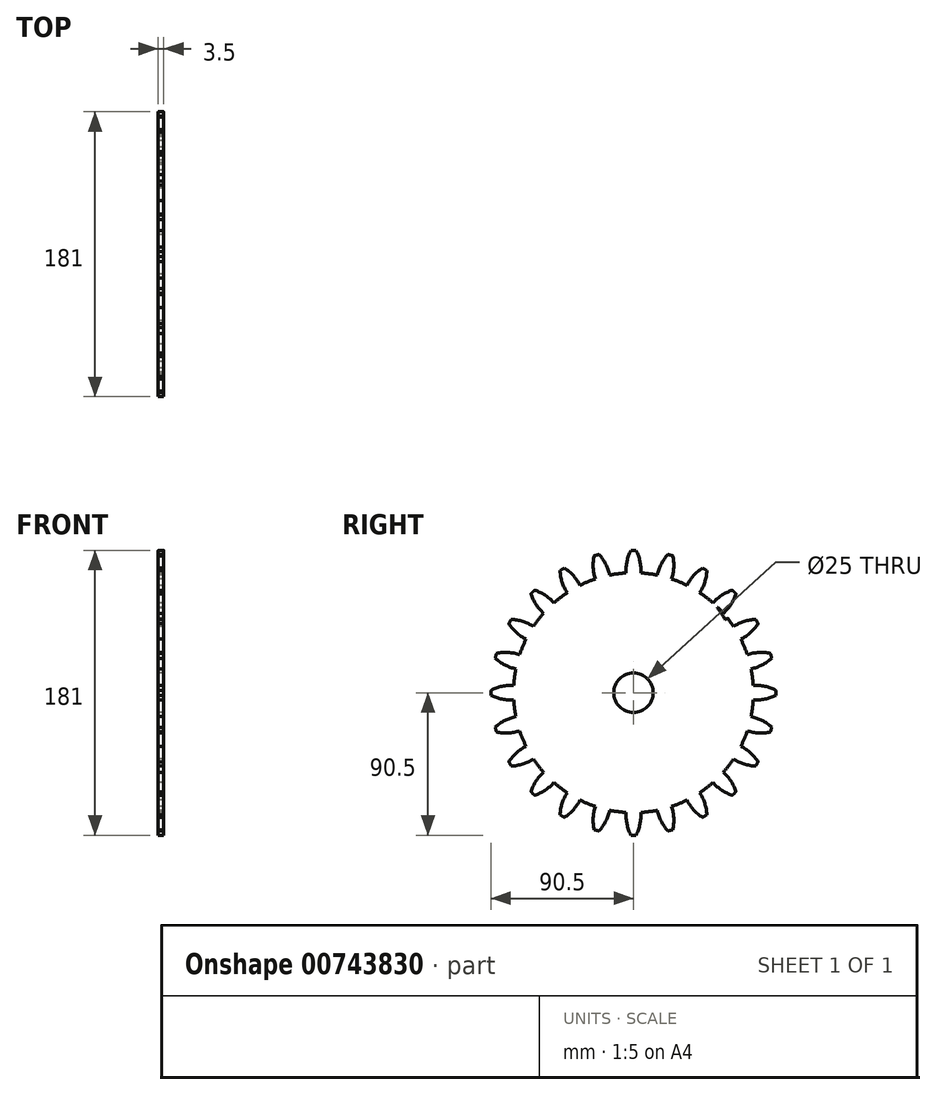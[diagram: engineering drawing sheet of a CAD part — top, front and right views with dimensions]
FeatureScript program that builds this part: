
annotation { "Feature Type Name" : "Feature", "Feature Type Description" : "" }
export const myFeature = defineFeature(function(context is Context, id is Id, definition is map)
    precondition{}
    {
        {
            assignVariable(context, id + "F0", {"name" : "FaceWidth", "anyValue" : 3.5});
        }
        {
            assignVariable(context, id + "F1", {"name" : "NumberTeeth", "anyValue" : 24});
        }
        {
            var Q0;
            Q0=qCreatedBy(makeId("Right.planeOp"),FACE);
            var sketch = newSketch(context, id + "F2", { "sketchPlane" : qUnion([Q0])});
            skCircle(sketch, "E0", {"center": v(0, 0) * mm, "radius": 76.2 * mm});
            skCircle(sketch, "E1", {"center": v(0, 0) * mm, "radius": 12.5 * mm});
            skCircle(sketch, "E2", {"center": v(0, 0) * mm, "radius": 90.5 * mm});
            skPoint(sketch, "E3", {"position": v(0, 76.2) * mm});
            skPoint(sketch, "E4", {"position": v(0, 84.15) * mm});
            skPoint(sketch, "E5", {"position": v(0, 90.5) * mm});
            skLineSegment(sketch, "E6", {"start": v(0, 76.2) * mm, "end": v(0, 84.15) * mm});
            skLineSegment(sketch, "E7", {"start": v(0, 90.5) * mm, "end": v(0, 84.15) * mm});
            skPoint(sketch, "E8", {"position": v(-5.53, 90.33) * mm});
            skLineSegment(sketch, "E9", {"start": v(-5.53, 90.33) * mm, "end": v(0, 0) * mm});
            skArc(sketch, "E10", {"start": v(-1.59, 90.49) * mm, "mid": v(-4.1, 83.48) * mm, "end": v(-4.65, 76.06) * mm});
            skArc(sketch, "E11.MirrorCS", {"start": v(1.59, 90.49) * mm, "mid": v(4.1, 83.48) * mm, "end": v(4.65, 76.06) * mm});
            skLineSegment(sketch, "E12.MirrorCS", {"start": v(5.53, 90.33) * mm, "end": v(0, 0) * mm});
            skPoint(sketch, "E13", {"position": v(-3.88, 84.43) * mm});
            skPoint(sketch, "E14", {"position": v(4.07, 83.64) * mm});
            skArc(sketch, "E15.1.0", {"start": v(-22.57, 89.12) * mm, "mid": v(-23.46, 81.73) * mm, "end": v(-22.35, 74.37) * mm});
            skArc(sketch, "E15.1.1", {"start": v(-19.48, 89.82) * mm, "mid": v(-15.47, 83.55) * mm, "end": v(-13.28, 76.44) * mm});
            skArc(sketch, "E15.2.0", {"start": v(-42.72, 83.1) * mm, "mid": v(-41.95, 75.7) * mm, "end": v(-39.22, 68.78) * mm});
            skArc(sketch, "E15.2.1", {"start": v(-39.86, 84.49) * mm, "mid": v(-34.56, 79.27) * mm, "end": v(-30.84, 72.82) * mm});
            skPoint(sketch, "E15.center", {"position": v(-6, -3.31) * mm});
            skArc(sketch, "E16.3.3.0", {"start": v(-61.03, 72.77) * mm, "mid": v(-58.63, 65.73) * mm, "end": v(-54.43, 59.58) * mm});
            skArc(sketch, "E16.4.3.0", {"start": v(-58.55, 74.75) * mm, "mid": v(-52.22, 70.84) * mm, "end": v(-47.16, 65.38) * mm});
            skArc(sketch, "E16.3.4.0", {"start": v(-76.58, 58.62) * mm, "mid": v(-72.67, 52.28) * mm, "end": v(-67.21, 47.22) * mm});
            skArc(sketch, "E16.4.4.0", {"start": v(-74.6, 61.1) * mm, "mid": v(-67.56, 58.7) * mm, "end": v(-61.41, 54.5) * mm});
            skArc(sketch, "E16.3.5.0", {"start": v(-88.6, 41.36) * mm, "mid": v(-83.37, 36.05) * mm, "end": v(-76.93, 32.33) * mm});
            skArc(sketch, "E16.4.5.0", {"start": v(-87.22, 44.22) * mm, "mid": v(-79.81, 43.44) * mm, "end": v(-72.89, 40.72) * mm});
            skArc(sketch, "E16.3.6.0", {"start": v(-96.46, 21.86) * mm, "mid": v(-90.2, 17.85) * mm, "end": v(-83.08, 15.66) * mm});
            skArc(sketch, "E16.4.6.0", {"start": v(-95.76, 24.95) * mm, "mid": v(-88.37, 25.84) * mm, "end": v(-81, 24.73) * mm});
            skArc(sketch, "E16.3.7.0", {"start": v(-99.8, 1.1) * mm, "mid": v(-92.8, -1.42) * mm, "end": v(-85.37, -1.97) * mm});
            skArc(sketch, "E16.4.7.0", {"start": v(-99.8, 4.27) * mm, "mid": v(-92.8, 6.78) * mm, "end": v(-85.37, 7.33) * mm});
            skArc(sketch, "E16.3.8.0", {"start": v(-98.43, -19.9) * mm, "mid": v(-91.04, -20.78) * mm, "end": v(-83.68, -19.67) * mm});
            skArc(sketch, "E16.4.8.0", {"start": v(-99.13, -16.8) * mm, "mid": v(-92.86, -12.78) * mm, "end": v(-85.75, -10.6) * mm});
            skArc(sketch, "E16.3.9.0", {"start": v(-92.42, -40.04) * mm, "mid": v(-85.02, -39.27) * mm, "end": v(-78.1, -36.54) * mm});
            skArc(sketch, "E16.4.9.0", {"start": v(-93.8, -37.18) * mm, "mid": v(-88.58, -31.88) * mm, "end": v(-82.13, -28.16) * mm});
            skArc(sketch, "E16.3.10.0", {"start": v(-82.08, -58.35) * mm, "mid": v(-75.04, -55.95) * mm, "end": v(-68.89, -51.75) * mm});
            skArc(sketch, "E16.4.10.0", {"start": v(-84.06, -55.87) * mm, "mid": v(-80.15, -49.54) * mm, "end": v(-74.7, -44.48) * mm});
            skArc(sketch, "E16.3.11.0", {"start": v(-67.93, -73.9) * mm, "mid": v(-61.6, -70) * mm, "end": v(-56.53, -64.53) * mm});
            skArc(sketch, "E16.4.11.0", {"start": v(-70.4, -71.92) * mm, "mid": v(-68, -64.88) * mm, "end": v(-63.8, -58.73) * mm});
            skArc(sketch, "E16.3.12.0", {"start": v(-50.67, -85.91) * mm, "mid": v(-45.36, -80.7) * mm, "end": v(-41.64, -74.24) * mm});
            skArc(sketch, "E16.4.12.0", {"start": v(-53.53, -84.54) * mm, "mid": v(-52.75, -77.13) * mm, "end": v(-50.03, -70.2) * mm});
            skArc(sketch, "E16.3.13.0", {"start": v(-31.17, -93.78) * mm, "mid": v(-27.16, -87.51) * mm, "end": v(-24.97, -80.4) * mm});
            skArc(sketch, "E16.4.13.0", {"start": v(-34.26, -93.08) * mm, "mid": v(-35.15, -85.69) * mm, "end": v(-34.04, -78.33) * mm});
            skArc(sketch, "E16.3.14.0", {"start": v(-10.4, -97.12) * mm, "mid": v(-7.89, -90.11) * mm, "end": v(-7.34, -82.69) * mm});
            skArc(sketch, "E16.4.14.0", {"start": v(-13.58, -97.12) * mm, "mid": v(-16.1, -90.11) * mm, "end": v(-16.64, -82.69) * mm});
            skArc(sketch, "E16.3.15.0", {"start": v(10.58, -95.75) * mm, "mid": v(11.47, -88.36) * mm, "end": v(10.36, -81) * mm});
            skArc(sketch, "E16.4.15.0", {"start": v(7.48, -96.45) * mm, "mid": v(3.47, -90.18) * mm, "end": v(1.29, -83.07) * mm});
            skArc(sketch, "E16.3.16.0", {"start": v(30.73, -89.74) * mm, "mid": v(29.96, -82.34) * mm, "end": v(27.23, -75.4) * mm});
            skArc(sketch, "E16.4.16.0", {"start": v(27.87, -91.12) * mm, "mid": v(22.57, -85.9) * mm, "end": v(18.85, -79.45) * mm});
            skArc(sketch, "E16.3.17.0", {"start": v(49.04, -79.4) * mm, "mid": v(46.64, -72.36) * mm, "end": v(42.44, -66.2) * mm});
            skArc(sketch, "E16.4.17.0", {"start": v(46.56, -81.38) * mm, "mid": v(40.23, -77.47) * mm, "end": v(35.17, -72.01) * mm});
            skArc(sketch, "E16.3.18.0", {"start": v(64.6, -65.25) * mm, "mid": v(60.68, -58.91) * mm, "end": v(55.22, -53.85) * mm});
            skArc(sketch, "E16.4.18.0", {"start": v(62.61, -67.73) * mm, "mid": v(55.57, -65.33) * mm, "end": v(49.42, -61.13) * mm});
            skArc(sketch, "E16.3.19.0", {"start": v(76.6, -47.99) * mm, "mid": v(71.38, -42.68) * mm, "end": v(64.93, -38.96) * mm});
            skArc(sketch, "E16.4.19.0", {"start": v(75.23, -50.85) * mm, "mid": v(67.82, -50.07) * mm, "end": v(60.9, -47.35) * mm});
            skArc(sketch, "E16.3.20.0", {"start": v(84.47, -28.49) * mm, "mid": v(78.2, -24.47) * mm, "end": v(71.09, -22.29) * mm});
            skArc(sketch, "E16.4.20.0", {"start": v(83.77, -31.58) * mm, "mid": v(76.38, -32.47) * mm, "end": v(69.02, -31.36) * mm});
            skArc(sketch, "E16.3.21.0", {"start": v(87.8, -7.72) * mm, "mid": v(80.8, -5.2) * mm, "end": v(73.38, -4.66) * mm});
            skArc(sketch, "E16.4.21.0", {"start": v(87.8, -10.9) * mm, "mid": v(80.8, -13.41) * mm, "end": v(73.38, -13.96) * mm});
            skArc(sketch, "E16.3.22.0", {"start": v(86.43, 13.26) * mm, "mid": v(79.05, 14.15) * mm, "end": v(71.69, 13.04) * mm});
            skArc(sketch, "E16.4.22.0", {"start": v(87.14, 10.16) * mm, "mid": v(80.87, 6.15) * mm, "end": v(73.76, 3.97) * mm});
            skArc(sketch, "E16.3.23.0", {"start": v(80.43, 33.41) * mm, "mid": v(73.03, 32.64) * mm, "end": v(66.1, 29.91) * mm});
            skArc(sketch, "E16.4.23.0", {"start": v(81.8, 30.55) * mm, "mid": v(76.59, 25.25) * mm, "end": v(70.14, 21.53) * mm});
            skArc(sketch, "E16.3.24.0", {"start": v(70.09, 51.72) * mm, "mid": v(63.04, 49.32) * mm, "end": v(56.9, 45.12) * mm});
            skArc(sketch, "E16.4.24.0", {"start": v(72.07, 49.24) * mm, "mid": v(68.16, 42.9) * mm, "end": v(62.7, 37.85) * mm});
            skArc(sketch, "E16.3.25.0", {"start": v(55.93, 67.27) * mm, "mid": v(49.6, 63.36) * mm, "end": v(44.54, 57.9) * mm});
            skArc(sketch, "E16.4.25.0", {"start": v(58.42, 65.3) * mm, "mid": v(56.02, 58.25) * mm, "end": v(51.82, 52.1) * mm});
            skArc(sketch, "E16.3.26.0", {"start": v(38.67, 79.28) * mm, "mid": v(33.37, 74.06) * mm, "end": v(29.65, 67.61) * mm});
            skArc(sketch, "E16.4.26.0", {"start": v(41.54, 77.9) * mm, "mid": v(40.76, 70.5) * mm, "end": v(38.04, 63.58) * mm});
            skArc(sketch, "E16.3.27.0", {"start": v(19.17, 87.15) * mm, "mid": v(15.16, 80.88) * mm, "end": v(12.98, 73.77) * mm});
            skArc(sketch, "E16.4.27.0", {"start": v(22.27, 86.45) * mm, "mid": v(23.16, 79.06) * mm, "end": v(22.05, 71.7) * mm});
            skArc(sketch, "E17.trimOffspring", {"start": v(-42.03, 76.03) * mm, "mid": v(-46.86, 73.3) * mm, "end": v(-51.48, 70.21) * mm});
            skArc(sketch, "E18.trimOffspring", {"start": v(15.25, 81.06) * mm, "mid": v(9.7, 82.56) * mm, "end": v(4.07, 83.64) * mm});
            skArc(sketch, "E19.trimOffspring", {"start": v(32.64, 73.08) * mm, "mid": v(27.98, 75.76) * mm, "end": v(23.13, 78.1) * mm});
            skArc(sketch, "E20.trimOffspring", {"start": v(47.25, 61.2) * mm, "mid": v(43.72, 64.65) * mm, "end": v(39.98, 67.87) * mm});
            skArc(sketch, "E21.trimOffspring", {"start": v(58.32, 46.33) * mm, "mid": v(55.95, 50.22) * mm, "end": v(53.35, 53.96) * mm});
            skArc(sketch, "E22.trimOffspring", {"start": v(65.36, 29.48) * mm, "mid": v(64.06, 33.64) * mm, "end": v(62.52, 37.72) * mm});
            skArc(sketch, "E23.trimOffspring", {"start": v(68.13, 11.72) * mm, "mid": v(67.84, 16.15) * mm, "end": v(67.3, 20.55) * mm});
            skArc(sketch, "E24.trimOffspring", {"start": v(66.69, -5.9) * mm, "mid": v(67.49, -1.16) * mm, "end": v(67.99, 3.63) * mm});
            skArc(sketch, "E25.trimOffspring", {"start": v(61.3, -22.43) * mm, "mid": v(63.41, -17.37) * mm, "end": v(65.14, -12.17) * mm});
            skArc(sketch, "E26.trimOffspring", {"start": v(52.53, -36.98) * mm, "mid": v(56.19, -31.79) * mm, "end": v(59.4, -26.3) * mm});
            skArc(sketch, "E27.trimOffspring", {"start": v(41.08, -48.9) * mm, "mid": v(46.47, -43.94) * mm, "end": v(51.34, -38.48) * mm});
            skArc(sketch, "E28.trimOffspring", {"start": v(27.87, -57.74) * mm, "mid": v(34.92, -53.52) * mm, "end": v(41.48, -48.56) * mm});
            skArc(sketch, "E29.trimOffspring", {"start": v(13.8, -63.42) * mm, "mid": v(22.19, -60.44) * mm, "end": v(30.16, -56.49) * mm});
            skArc(sketch, "E30.trimOffspring", {"start": v(-0.36, -66.11) * mm, "mid": v(8.77, -64.7) * mm, "end": v(17.66, -62.2) * mm});
            skArc(sketch, "E31.trimOffspring", {"start": v(-14.19, -66.12) * mm, "mid": v(-4.98, -66.4) * mm, "end": v(4.18, -65.56) * mm});
            skArc(sketch, "E32.trimOffspring", {"start": v(-27.45, -63.69) * mm, "mid": v(-18.82, -65.55) * mm, "end": v(-10.03, -66.38) * mm});
            skArc(sketch, "E33.trimOffspring", {"start": v(-40.02, -58.96) * mm, "mid": v(-32.47, -62.1) * mm, "end": v(-24.63, -64.41) * mm});
            skArc(sketch, "E34.trimOffspring", {"start": v(-51.72, -51.97) * mm, "mid": v(-45.58, -56) * mm, "end": v(-39.08, -59.4) * mm});
            skArc(sketch, "E35.trimOffspring", {"start": v(-62.25, -42.68) * mm, "mid": v(-57.65, -47.17) * mm, "end": v(-52.67, -51.26) * mm});
            skArc(sketch, "E36.trimOffspring", {"start": v(-71.2, -31.1) * mm, "mid": v(-68.06, -35.7) * mm, "end": v(-64.6, -40.07) * mm});
            skArc(sketch, "E37.trimOffspring", {"start": v(-78.01, -17.3) * mm, "mid": v(-76.16, -21.82) * mm, "end": v(-74.02, -26.2) * mm});
            skArc(sketch, "E38.trimOffspring", {"start": v(-82, -1.56) * mm, "mid": v(-81.26, -5.93) * mm, "end": v(-80.25, -10.25) * mm});
            skArc(sketch, "E39.trimOffspring", {"start": v(-82.47, 15.56) * mm, "mid": v(-82.72, 11.3) * mm, "end": v(-82.73, 7.04) * mm});
            skArc(sketch, "E40.trimOffspring", {"start": v(-78.79, 33.18) * mm, "mid": v(-80.07, 29) * mm, "end": v(-81.1, 24.76) * mm});
            skArc(sketch, "E41.trimOffspring", {"start": v(-70.63, 50.06) * mm, "mid": v(-73.06, 46.04) * mm, "end": v(-75.23, 41.89) * mm});
            skArc(sketch, "E42.trimOffspring", {"start": v(-58.14, 64.8) * mm, "mid": v(-61.81, 61.21) * mm, "end": v(-65.23, 57.39) * mm});
            skArc(sketch, "E43.trimOffspring", {"start": v(-3.88, 84.43) * mm, "mid": v(-9.8, 84.46) * mm, "end": v(-15.7, 84.03) * mm});
            skSolve(sketch);
        }
        {
            var Q0;
            {var subQ0=sQuery(id+"F2.wireOp",EDGE,"E9");var subQ5=sQuery(id+"F2.wireOp",EDGE,"E1");var subQ7=makeQuery(id+"F2.imprint","INTERSECT",VERTEX,{"derivedFrom":[subQ5,subQ0]});Q0=makeQuery(id+"F2.imprint","IMPRINT",FACE,{"disambiguationData":[TD([[makeQuery(id+"F2.imprint","IMPRINT",EDGE,{"disambiguationData":[TD([[subQ7,-1.0]])],"derivedFrom":subQ5}),-1.0]])]});}
            var Q1;
            {var subQ0=sQuery(id+"F2.wireOp",EDGE,"E9");var subQ3=sQuery(id+"F2.wireOp",EDGE,"E1");var subQ4=makeQuery(id+"F2.imprint","INTERSECT",VERTEX,{"derivedFrom":[subQ3,subQ0]});Q1=makeQuery(id+"F2.imprint","IMPRINT",FACE,{"disambiguationData":[TD([[makeQuery(id+"F2.imprint","IMPRINT",EDGE,{"disambiguationData":[TD([[subQ4,1.0]])],"derivedFrom":subQ3}),-1.0]])]});}
            extrude(context, id + "F3", {"entities" : qUnion([Q0, Q1]), "endBound" : BoundingType.SYMMETRIC, "depth" : (getVariable(context, 'FaceWidth')) * mm, "offsetDistance" : 25.4 * mm});
        }
        {
            var Q0;
            {var subQ0=sQuery(id+"F2.wireOp",EDGE,"E6");Q0=makeQuery(id+"F2.imprint","IMPRINT",FACE,{"disambiguationData":[TD([[makeQuery(id+"F2.imprint","IMPRINT",EDGE,{"derivedFrom":subQ0}),1.0]])]});}
            var Q1;
            {var subQ1=sQuery(id+"F2.wireOp",EDGE,"E6");Q1=makeQuery(id+"F2.imprint","IMPRINT",FACE,{"disambiguationData":[TD([[makeQuery(id+"F2.imprint","IMPRINT",EDGE,{"derivedFrom":subQ1}),-1.0]])]});}
            extrude(context, id + "F4", {"entities" : qUnion([Q0, Q1]), "endBound" : BoundingType.SYMMETRIC, "depth" : (getVariable(context, 'FaceWidth')) * mm, "offsetDistance" : 25.4 * mm});
        }
        {
            var Q0;
            Q0=makeQuery(id+"F4.opExtrude","SWEPT_BODY",BODY,{"disambiguationData":[OSD([sQuery(id+"F2.wireOp",EDGE,"E0"),sQuery(id+"F2.wireOp",EDGE,"E2"),sQuery(id+"F2.wireOp",EDGE,"E10"),sQuery(id+"F2.wireOp",EDGE,"E11.MirrorCS")])]});
            var Q1;
            Q1=makeQuery(id+"F3.opExtrude","SWEPT_FACE",FACE,{"disambiguationData":[OSD([sQuery(id+"F2.wireOp",EDGE,"E1")])]});
            circularPattern(context, id + "F5", {"operationType" : NewBodyOperationType.ADD, "entities" : qUnion([Q0]), "axis" : qUnion([Q1]), "angle" : 360 * degree, "instanceCount" : getVariable(context, 'NumberTeeth'), "equalSpace" : true});
        }
    });
